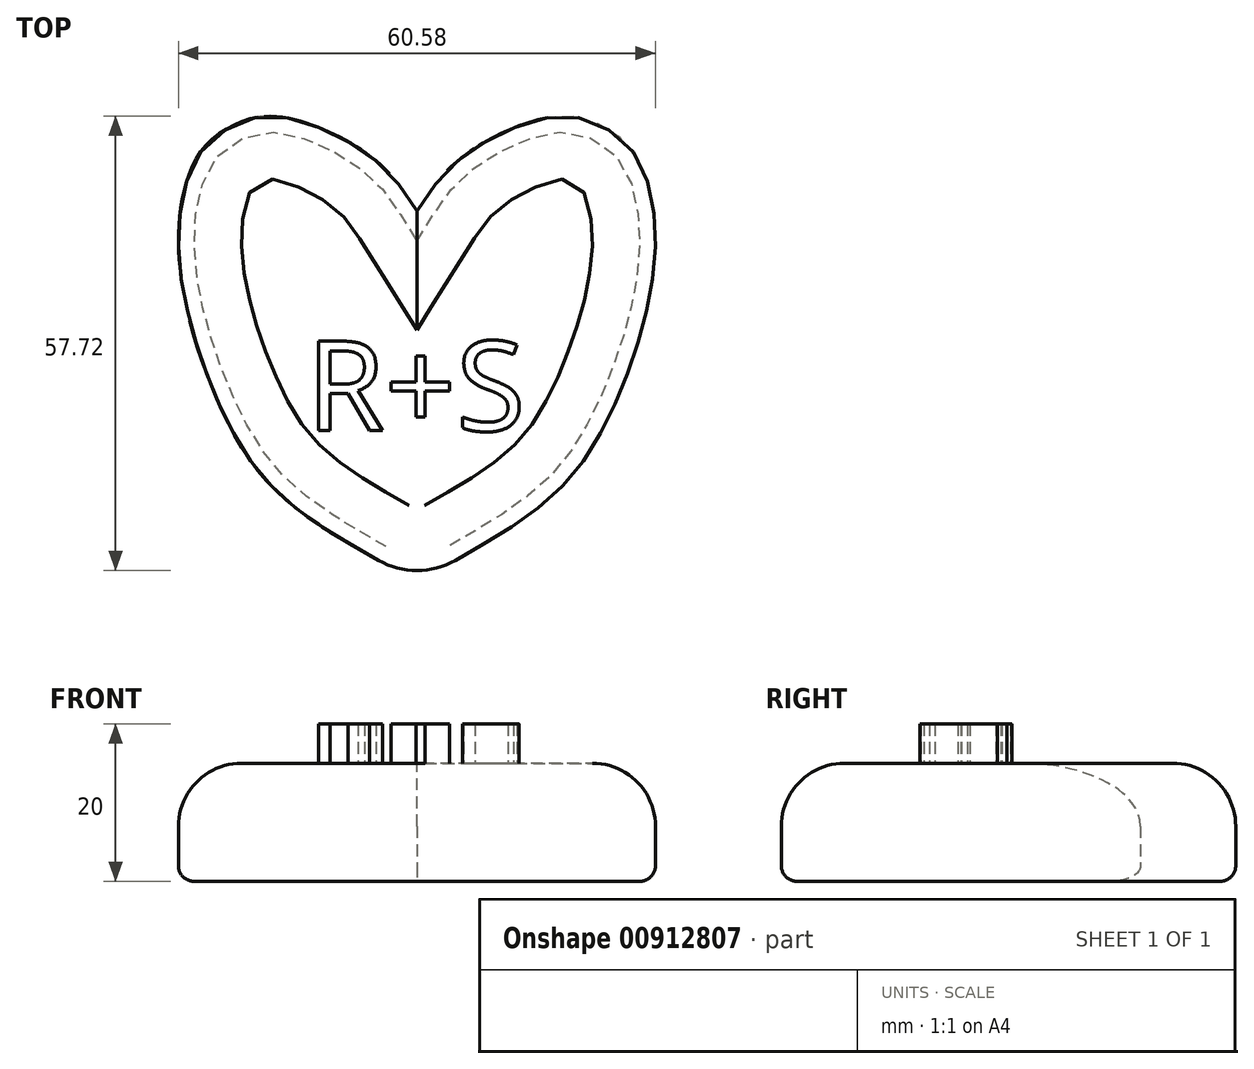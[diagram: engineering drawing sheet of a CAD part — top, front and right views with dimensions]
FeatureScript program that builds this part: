
annotation { "Feature Type Name" : "Feature", "Feature Type Description" : "" }
export const myFeature = defineFeature(function(context is Context, id is Id, definition is map)
    precondition{}
    {
        {
            var Q0;
            Q0=qCreatedBy(makeId("Top.planeOp"),FACE);
            var sketch = newSketch(context, id + "F0", { "sketchPlane" : qUnion([Q0])});
            skFitSpline(sketch, "E0", {"points": [v(0, -30) * mm, v(14.86, -21.05) * mm, v(23.06, -11.58) * mm, v(30.17, 10.48) * mm, v(27.98, 23.79) * mm, v(23.97, 27.62) * mm, v(17.6, 29.08) * mm, v(5.38, 23.6) * mm, v(0, 17.04) * mm], "startDerivative": vector(108.06, 58.97) * mm, "endDerivative": vector(-39.67, -63.53) * mm});
            skFitSpline(sketch, "E1.MirrorCS", {"points": [v(0, -30) * mm, v(-14.86, -21.05) * mm, v(-23.06, -11.58) * mm, v(-30.17, 10.48) * mm, v(-27.98, 23.79) * mm, v(-23.97, 27.62) * mm, v(-17.6, 29.08) * mm, v(-5.38, 23.6) * mm, v(0, 17.04) * mm], "startDerivative": vector(-108.06, 58.97) * mm, "endDerivative": vector(39.67, -63.53) * mm});
            skSolve(sketch);
        }
        {
            var Q0;
            Q0=makeQuery(id+"F0.imprint","IMPRINT",FACE,{"disambiguationData":[TD([[makeQuery(id+"F0.imprint","IMPRINT",EDGE,{"derivedFrom":sQuery(id+"F0.wireOp",EDGE,"E0")}),1.0]])]});
            extrude(context, id + "F1", {"entities" : qUnion([Q0]), "depth" : 15 * mm, "offsetDistance" : 25 * mm});
        }
        {
            var Q0;
            Q0=makeQuery(id+"F1.opExtrude","CAP_EDGE",EDGE,{"disambiguationData":[OSD([sQuery(id+"F0.wireOp",EDGE,"E0")])],"isStart":false});
            var Q1;
            Q1=makeQuery(id+"F1.opExtrude","CAP_EDGE",EDGE,{"disambiguationData":[OSD([sQuery(id+"F0.wireOp",EDGE,"E1.MirrorCS")])],"isStart":false});
            fillet(context, id + "F2", {"entities" : qUnion([Q0, Q1]), "radius" : 8 * mm, "tangentPropagation" : true, "allowEdgeOverflow" : false});
        }
        {
            var Q0;
            Q0=makeQuery(id+"F1.opExtrude","CAP_EDGE",EDGE,{"disambiguationData":[OSD([sQuery(id+"F0.wireOp",EDGE,"E1.MirrorCS")])],"isStart":true});
            var Q1;
            Q1=makeQuery(id+"F1.opExtrude","CAP_EDGE",EDGE,{"disambiguationData":[OSD([sQuery(id+"F0.wireOp",EDGE,"E0")])],"isStart":true});
            fillet(context, id + "F3", {"entities" : qUnion([Q0, Q1]), "radius" : 2 * mm, "tangentPropagation" : true, "allowEdgeOverflow" : false});
        }
        {
            var Q0;
            {var subQ0=sQuery(id+"F0.wireOp",EDGE,"E1.MirrorCS");var subQ1=sQuery(id+"F0.wireOp",EDGE,"E0");Q0=makeQuery(id+"F1.opExtrude","SWEPT_EDGE",EDGE,{"disambiguationData":[OSD([subQ1,subQ0]),TDD([makeQuery(id+"F0.imprint","INTERSECT",VERTEX,{"disambiguationData":[OD(0.0)],"derivedFrom":[subQ1,subQ0]})])]});}
            fillet(context, id + "F4", {"entities" : qUnion([Q0]), "radius" : 10 * mm, "tangentPropagation" : true, "allowEdgeOverflow" : false});
        }
        {
            var Q0;
            Q0=makeQuery(id+"F1.opExtrude","CAP_FACE",FACE,{"disambiguationData":[OSD([sQuery(id+"F0.wireOp",EDGE,"E0"),sQuery(id+"F0.wireOp",EDGE,"E1.MirrorCS")])],"isStart":false});
            var sketch = newSketch(context, id + "F5", { "sketchPlane" : qUnion([Q0])});
            skText(sketch, "E2", { "text": "R+S", "fontName": "NotoSans-Regular.ttf"});
            const initialGuessF5  = {"E2": [-0.01402, -0.01084, 1, 0, 0.01147]};
            skSetInitialGuess(sketch, initialGuessF5);
            skSolve(sketch);
        }
        {
            var Q0;
            Q0 = qSketchRegion(id + "F5", true);
            extrude(context, id + "F6", {"entities" : qUnion([Q0]), "operationType" : NewBodyOperationType.ADD, "depth" : 5 * mm, "offsetDistance" : 25 * mm});
        }
    });
